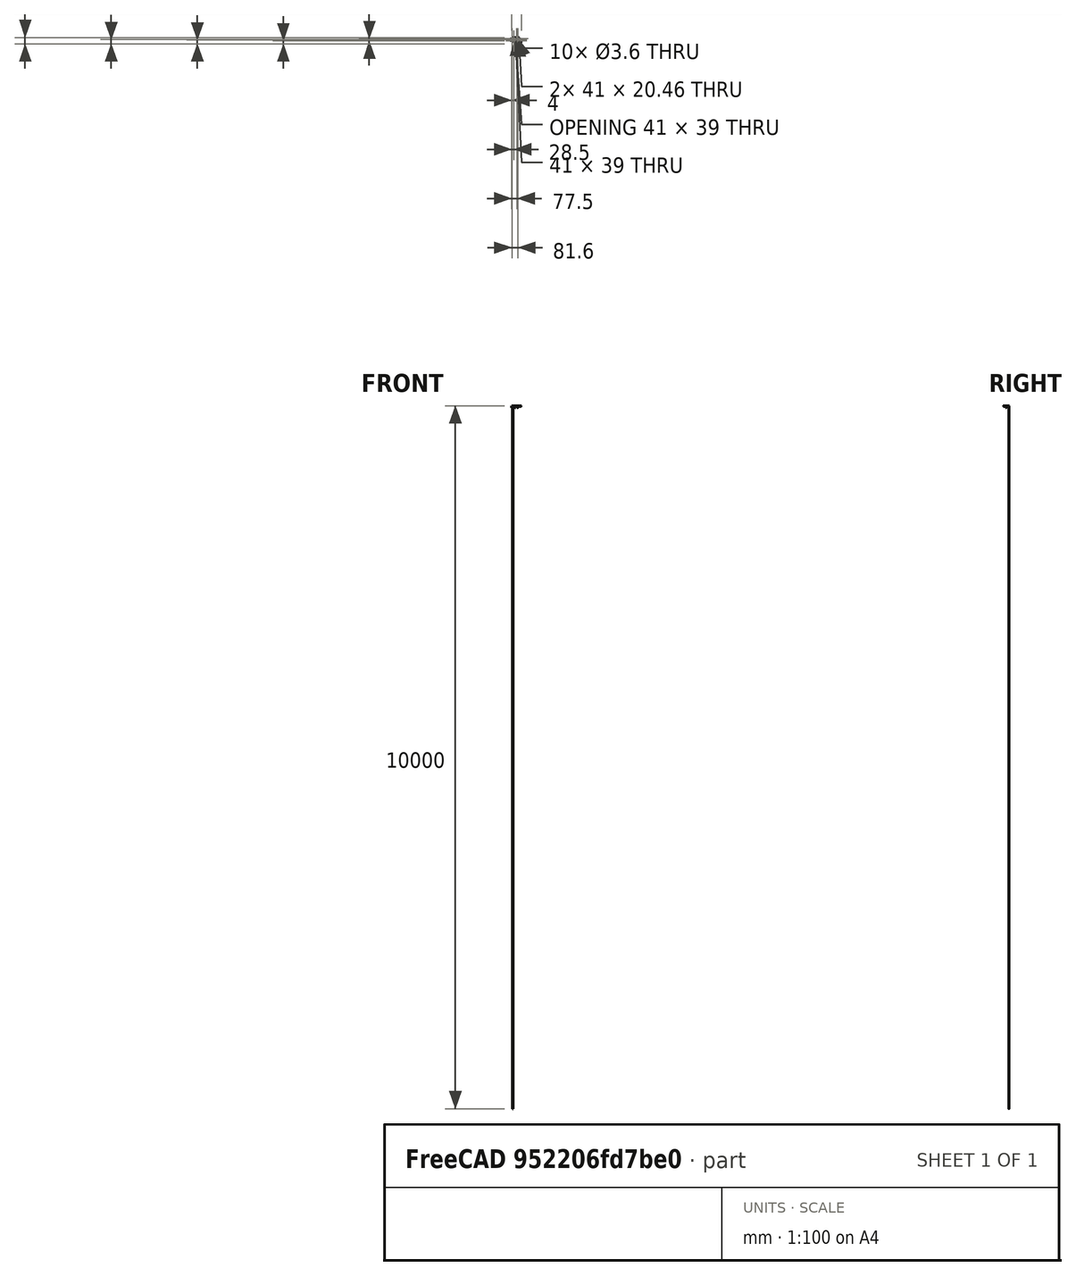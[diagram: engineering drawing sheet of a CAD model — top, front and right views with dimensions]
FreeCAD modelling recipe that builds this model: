
FCSTD DOCUMENT  (FreeCAD 0.14R3700 (Git))
Label: arduino platform
License: CC-BY 3.0
LicenseURL: http://creativecommons.org/licenses/by/3.0/
objects: Sketcher::SketchObject×4, PartDesign::Pad×2, PartDesign::Pocket×2
note: 12 computed .brp shape members not serialized (recipe doc carries the construction recipe); baked Part::Feature solids carry a one-line shape summary decoded from their .brp

FEATURE [Sketcher::SketchObject] Sketch
  Support = -> Pocket [Face5]
  sketch-geometry (24):
    g0: LineSegment StartX=-53 StartY=16 StartZ=0 EndX=53 EndY=16 EndZ=0
    g1: LineSegment StartX=-53 StartY=-39 StartZ=0 EndX=-53 EndY=16 EndZ=0
    g2: LineSegment StartX=-45 StartY=8 StartZ=0 EndX=-4 EndY=8 EndZ=0
    g3: LineSegment StartX=45 StartY=-27 StartZ=0 EndX=4 EndY=-27 EndZ=0
    g4: LineSegment StartX=-45 StartY=-31 StartZ=0 EndX=-45 EndY=8 EndZ=0
    g5: Circle CenterX=-49 CenterY=0 CenterZ=0 NormalX=0 NormalY=0 NormalZ=1 Radius=1.8
    g6: Circle CenterX=32.6 CenterY=0 CenterZ=0 NormalX=0 NormalY=0 NormalZ=1 Radius=1.8
    g7: LineSegment StartX=-4 StartY=-31 StartZ=0 EndX=-4 EndY=8 EndZ=0
    g8: LineSegment StartX=-4 StartY=-31 StartZ=0 EndX=-45 EndY=-31 EndZ=0
    g9: LineSegment StartX=53 StartY=-7.61453 StartZ=0 EndX=85.5269 EndY=-40.1414 EndZ=0
    g10: LineSegment StartX=85.5269 StartY=-40.1414 StartZ=0 EndX=55.1213 EndY=-72.5289 EndZ=0
    g11: LineSegment StartX=55.1213 StartY=-72.5289 StartZ=0 EndX=19.1268 EndY=-38.737 EndZ=0
    g12: LineSegment StartX=-53 StartY=-39 StartZ=0 EndX=19.1268 EndY=-38.737 EndZ=0
    g13: LineSegment StartX=53 StartY=16 StartZ=0 EndX=53 EndY=-7.61453 EndZ=0
    g14: LineSegment StartX=4 StartY=-6.53698 StartZ=0 EndX=45 EndY=-6.53698 EndZ=0
    g15: LineSegment StartX=4 StartY=-6.53698 StartZ=0 EndX=4 EndY=-27 EndZ=0
    g16: LineSegment StartX=45 StartY=-6.53698 StartZ=0 EndX=45 EndY=-27 EndZ=0
    g17: GeomPoint [constr] X=21.1337 Y=29.9692 Z=0
    g18: ArcOfCircle CenterX=-39.2 CenterY=-36 CenterZ=0 NormalX=0 NormalY=0 NormalZ=1 Radius=1.8 StartAngle=1.57081 EndAngle=4.71238
    g19: ArcOfCircle CenterX=-36.2 CenterY=-36 CenterZ=0 NormalX=0 NormalY=0 NormalZ=1 Radius=1.8 StartAngle=4.71239 EndAngle=7.85398
    g20: LineSegment StartX=-39.2 StartY=-37.8 StartZ=0 EndX=-36.2 EndY=-37.8 EndZ=0
    g21: LineSegment StartX=-39.2 StartY=-34.2 StartZ=0 EndX=-36.2 EndY=-34.2 EndZ=0
    g22: Circle CenterX=13.2 CenterY=-30.537 CenterZ=0 NormalX=0 NormalY=0 NormalZ=1 Radius=1.8
    g23: Circle CenterX=13.2 CenterY=-2.53698 CenterZ=0 NormalX=0 NormalY=0 NormalZ=1 Radius=1.8
  constraints (71):
    c: Coincident(g1,g0)
    c: Horizontal(g0)
    c: Vertical(g1)
    c: DistanceX(g0,g0) = 106
    c: DistanceX(g-1,g1) = -53
    c: Coincident(g8,g4)
    c: Coincident(g4,g2)
    c: Horizontal(g2)
    c: Horizontal(g3)
    c: Vertical(g4)
    c: DistanceX(g8,g1) = -8
    c: DistanceY(g1,g8) = 8
    c: DistanceY(g-1,g0) = 16
    c: Radius(g5) = 1.8
    c: DistanceX(g5,g2) = 4
    c: DistanceY(g-1,g5) = 0
    c: Radius(g6) = 1.8
    c: DistanceY(g-1,g6) = 0
    c: Vertical(g7)
    c: Equal(g4,g7)
    c: Equal(g8,g2)
    c: DistanceY(g2,g0) = 8
    c: DistanceX(g7,g3) = 8
    c: Coincident(g9,g10)
    c: Coincident(g10,g11)
    c: Angle(g10,g11) = 1.5708
    c: Horizontal(g8)
    c: Coincident(g7,g8)
    c: DistanceY(g0,g1) = -55
    c: Distance(g11,g9) = 46
    c: Coincident(g11,g12)
    c: Coincident(g1,g12)
    c: Coincident(g9,g13)
    c: Coincident(g0,g13)
    c: Angle(g9,g13) = 2.35619
    c: Distance(g9,g9) = 46
    c: Vertical(g13)
    c: DistanceX(g1,g11) = 72.1268
    c: Horizontal(g14)
    c: Vertical(g15)
    c: Coincident(g3,g15)
    c: Coincident(g3,g16)
    c: Coincident(g14,g16)
    c: Tangent(g18,g20)
    c: Tangent(g18,g21)
    c: Tangent(g19,g20)
    c: Tangent(g19,g21)
    c: Coincident(g18,g21)
    c: Coincident(g18,g20)
    c: Coincident(g20,g19)
    c: Coincident(g21,g19)
    c: Horizontal(g20)
    c: Equal(g18,g19)
    c: Radius(g18) = 1.8
    c: DistanceX(g1,g18) = 13.8
    c: DistanceX(g18,g19) = 3
    c: Radius(g22) = 1.8
    c: DistanceY(g22,g11) = -8.2
    c: DistanceX(g18,g22) = 52.4
    c: Radius(g23) = 1.8
    c: DistanceY(g22,g23) = 28
    c: DistanceX(g22,g23) = 0
    c: Coincident(g14,g15)
    c: DistanceY(g14,g3) = -20.463
    c: Vertical(g16)
    c: Equal(g15,g16)
    c: Equal(g14,g3)
    c: DistanceX(g14,g14) = 41
    c: DistanceX(g10) = 55.1213
    c: DistanceY(g10) = -72.5289
    c: DistanceX(g6,g5) = -81.6
FEATURE [Sketcher::SketchObject] Sketch001
  Placement = pos=(0,0,0) rot=(1,0,0;3.14159rad)
  Support = -> Pad [Face24]
  sketch-geometry (5):
    g0: Circle CenterX=0 CenterY=28 CenterZ=0 NormalX=0 NormalY=0 NormalZ=1 Radius=3.8
    g1: Circle CenterX=-49 CenterY=0 CenterZ=0 NormalX=0 NormalY=0 NormalZ=1 Radius=4
    g2: Circle CenterX=32.6 CenterY=0 CenterZ=0 NormalX=0 NormalY=0 NormalZ=1 Radius=4
    g3: Circle CenterX=-49 CenterY=0 CenterZ=0 NormalX=0 NormalY=0 NormalZ=1 Radius=1.8
    g4: Circle CenterX=32.6 CenterY=0 CenterZ=0 NormalX=0 NormalY=0 NormalZ=1 Radius=1.8
  constraints (12):
    c: Radius(g0) = 3.8
    c: DistanceY(g-1,g0) = 28
    c: DistanceX(g-1,g0) = 0
    c: Radius(g1) = 4
    c: Radius(g2) = 4
    c: Radius(g3) = 1.8
    c: Coincident(g3,g1)
    c: Radius(g4) = 1.8
    c: Coincident(g4,g2)
    c: DistanceX(g1) = -49
    c: DistanceY(g1) = 0
    c: DistanceX(g1,g2) = 81.6
FEATURE [PartDesign::Pad] Pad
  Length = 2
  Length2 = 20
  Sketch = -> Sketch
  Type = 0
FEATURE [Sketcher::SketchObject] Sketch002
  Placement = pos=(0,0,2) rot=(0,0,1;0rad)
  Support = -> Pad001 [Face5]
  sketch-geometry (8):
    g0: Circle CenterX=53.4328 CenterY=-58.2562 CenterZ=0 NormalX=0 NormalY=0 NormalZ=1 Radius=8.25
    g1: Circle CenterX=71.4338 CenterY=-39.0818 CenterZ=0 NormalX=0 NormalY=0 NormalZ=1 Radius=8.25
    g2: ArcOfCircle CenterX=66.1408 CenterY=-56.1562 CenterZ=0 NormalX=0 NormalY=0 NormalZ=1 Radius=2.19658 StartAngle=2.3562 EndAngle=5.49779
    g3: ArcOfCircle CenterX=70.737 CenterY=-51.56 CenterZ=0 NormalX=0 NormalY=0 NormalZ=1 Radius=2.19658 StartAngle=5.49779 EndAngle=8.63938
    g4: LineSegment StartX=67.7757 StartY=-57.6277 StartZ=0 EndX=72.405 EndY=-52.9984 EndZ=0
    g5: LineSegment StartX=64.4376 StartY=-54.7529 StartZ=0 EndX=69.0669 EndY=-50.1236 EndZ=0
    g6: LineSegment [constr] StartX=66.1408 StartY=-56.1562 StartZ=0 EndX=70.737 EndY=-51.56 EndZ=0
    g7: LineSegment [constr] StartX=66.1408 StartY=-56.1562 StartZ=0 EndX=78.7573 EndY=-56.1562 EndZ=0
  constraints (18):
    c: DistanceX(g0) = 53.4328
    c: DistanceY(g0) = -58.2562
    c: DistanceX(g1) = 71.4338
    c: DistanceY(g1) = -39.0818
    c: Radius(g0) = 8.25
    c: Radius(g1) = 8.25
    c: Tangent(g2,g5)
    c: Tangent(g3,g5)
    c: Tangent(g2,g4)
    c: Tangent(g3,g4)
    c: Distance(g2,g3) = 6.5
    c: DistanceX(g2,g0) = -12.708
    c: DistanceY(g2,g0) = -2.1
    c: Parallel(g4,g5)
    c: Horizontal(g7)
    c: Angle(g7,g6) = 0.785398
    c: Coincident(g3,g6)
    c: Coincident(g6,g2)
FEATURE [Sketcher::SketchObject] Sketch003
  Placement = pos=(0,0,2) rot=(0,0,1;0rad)
  Support = -> Pocket [Face5]
  sketch-geometry (1):
    g0: Circle CenterX=-38 CenterY=12 CenterZ=0 NormalX=0 NormalY=0 NormalZ=1 Radius=1.8
  constraints (1):
    c: Radius(g0) = 1.8
FEATURE [PartDesign::Pad] Pad001
  Length = 24
  Length2 = 20
  Sketch = -> Sketch001
  Type = 0
FEATURE [PartDesign::Pocket] Pocket
  Length = 5
  Sketch = -> Sketch002
  Type = 0
FEATURE [PartDesign::Pocket] Pocket001
  Length = 5
  Sketch = -> Sketch003
  Type = 1
